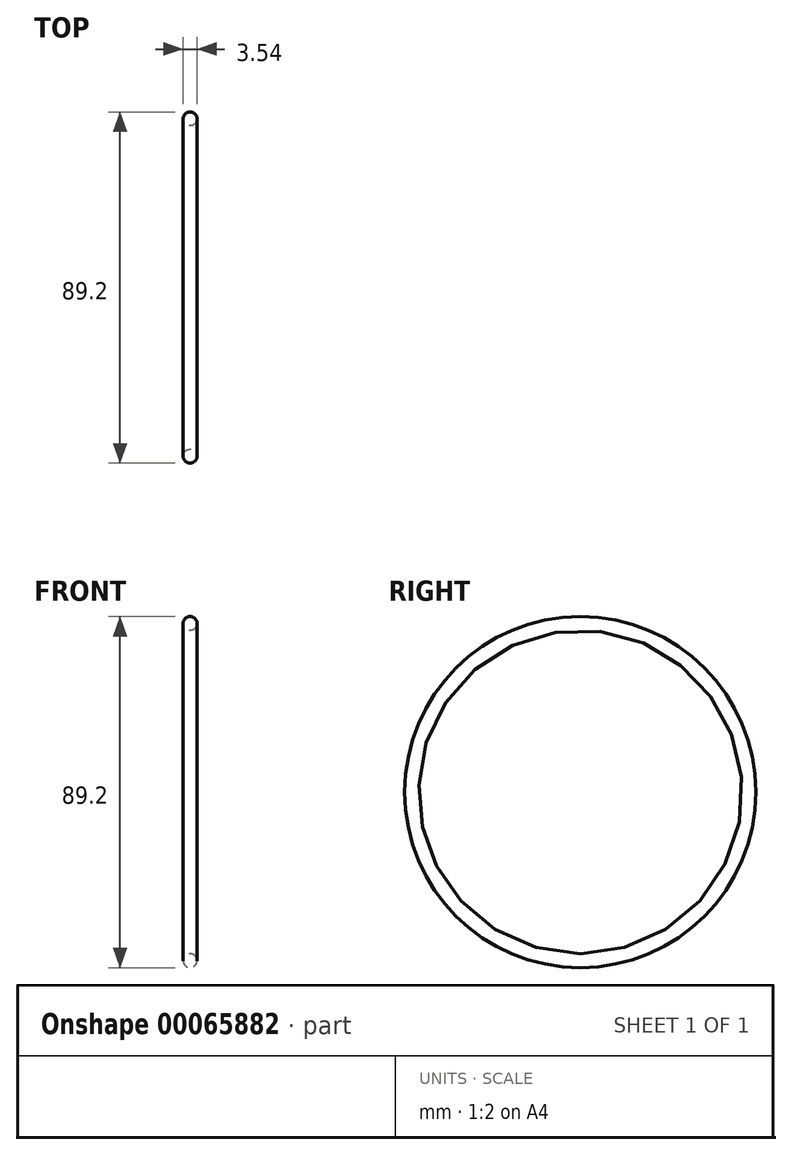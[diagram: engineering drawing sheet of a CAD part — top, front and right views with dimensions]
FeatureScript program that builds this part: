
annotation { "Feature Type Name" : "Feature", "Feature Type Description" : "" }
export const myFeature = defineFeature(function(context is Context, id is Id, definition is map)
    precondition{}
    {
        {
            var Q0;
            Q0=qCreatedBy(makeId("Front.planeOp"),FACE);
            var sketch = newSketch(context, id + "F0", { "sketchPlane" : qUnion([Q0])});
            skLineSegment(sketch, "E0", {"start": v(0, 0) * mm, "end": v(-6.06, 0) * mm, "construction": true});
            skCircle(sketch, "E1", {"center": v(0, 42.84) * mm, "radius": 1.77 * mm});
            skSolve(sketch);
        }
        {
            var Q0;
            Q0=makeQuery(id+"F0.imprint","IMPRINT",FACE,{"disambiguationData":[TD([[makeQuery(id+"F0.imprint","IMPRINT",EDGE,{"derivedFrom":sQuery(id+"F0.wireOp",EDGE,"E1")}),1.0]])]});
            var Q1;
            Q1=sQuery(id+"F0.wireOp",EDGE,"E0");
            revolve(context, id + "F1", {"entities" : qUnion([Q0]), "axis" : qUnion([Q1]), "revolveType" : RevolveType.FULL});
        }
    });
